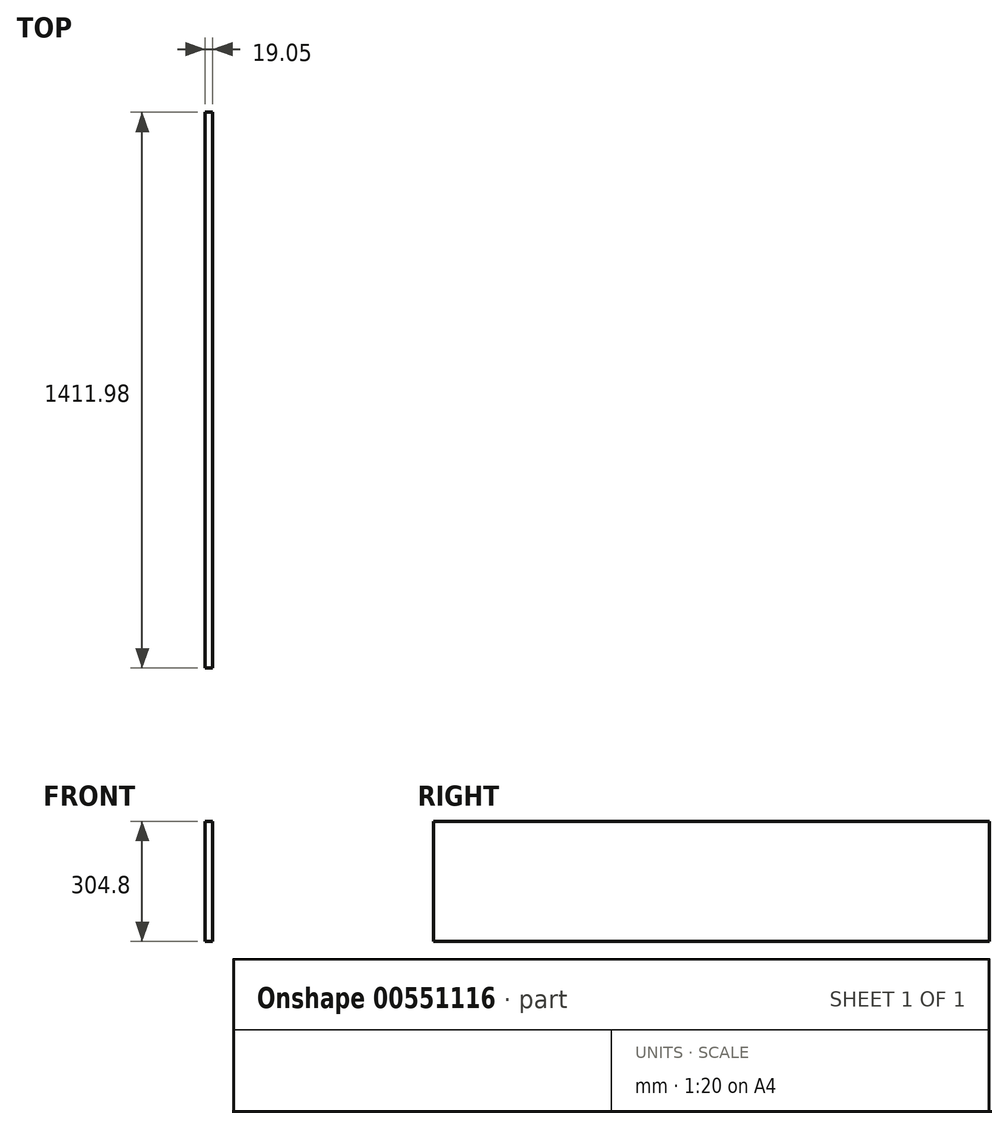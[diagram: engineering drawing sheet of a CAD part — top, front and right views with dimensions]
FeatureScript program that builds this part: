
annotation { "Feature Type Name" : "Feature", "Feature Type Description" : "" }
export const myFeature = defineFeature(function(context is Context, id is Id, definition is map)
    precondition{}
    {
        {
            var Q0;
            Q0=qCreatedBy(makeId("Right.planeOp"),FACE);
            var sketch = newSketch(context, id + "F0", { "sketchPlane" : qUnion([Q0])});
            skLineSegment(sketch, "E0.bottom", {"start": v(858.4, 152.4) * mm, "end": v(-858.4, 152.4) * mm});
            skLineSegment(sketch, "E0.top", {"start": v(858.4, -152.4) * mm, "end": v(-858.4, -152.4) * mm});
            skLineSegment(sketch, "E0.left", {"start": v(858.4, 152.4) * mm, "end": v(858.4, -152.4) * mm});
            skLineSegment(sketch, "E0.right", {"start": v(-858.4, 152.4) * mm, "end": v(-858.4, -152.4) * mm});
            skPoint(sketch, "E0.middle", {"position": v(0, 0) * mm});
            skSolve(sketch);
        }
        {
            var Q0;
            Q0 = qSketchRegion(id + "F0", true);
            extrude(context, id + "F1", {"entities" : qUnion([Q0]), "depth" : 19.05 * mm, "offsetDistance" : 25.4 * mm});
        }
        {
            var Q0;
            Q0=makeQuery(id+"F1.opExtrude","SWEPT_FACE",FACE,{"disambiguationData":[OSD([sQuery(id+"F0.wireOp",EDGE,"E0.left")])]});
            extrude(context, id + "F2", {"entities" : qUnion([Q0]), "operationType" : NewBodyOperationType.REMOVE, "oppositeDirection" : true, "depth" : 304.8 * mm, "offsetDistance" : 25.4 * mm});
        }
    });
